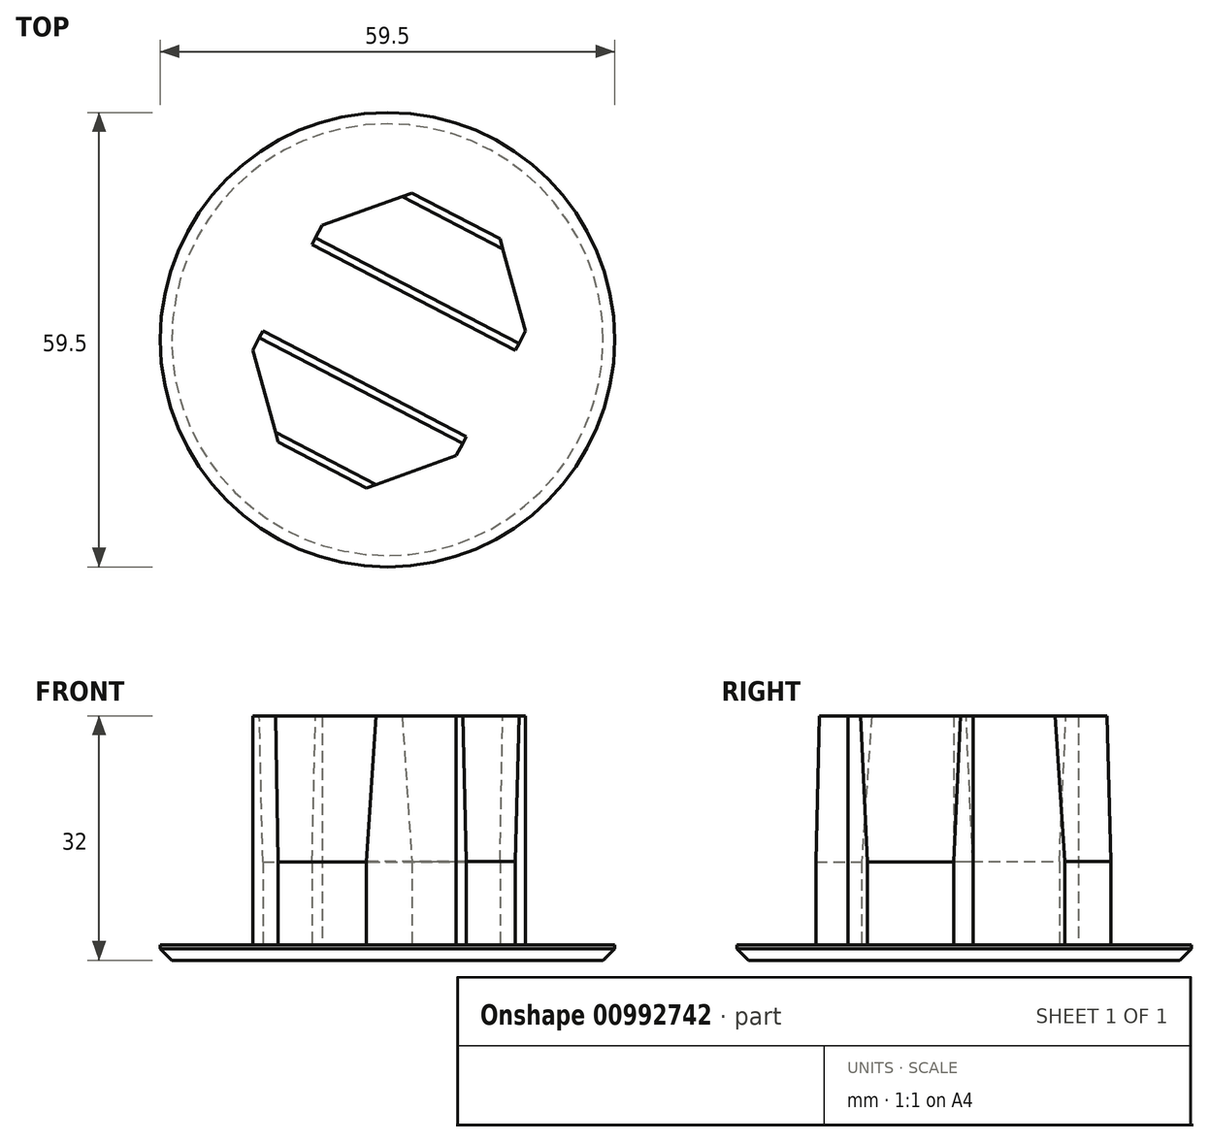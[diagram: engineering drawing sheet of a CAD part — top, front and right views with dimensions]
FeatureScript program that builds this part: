
annotation { "Feature Type Name" : "Feature", "Feature Type Description" : "" }
export const myFeature = defineFeature(function(context is Context, id is Id, definition is map)
    precondition{}
    {
        {
            var Q0;
            Q0=qCreatedBy(makeId("Top.planeOp"),FACE);
            var sketch = newSketch(context, id + "F0", { "sketchPlane" : qUnion([Q0])});
            skCircle(sketch, "E0", {"center": v(0, 0) * mm, "radius": 29.75 * mm});
            skSolve(sketch);
        }
        {
            var Q0;
            Q0 = qSketchRegion(id + "F0", true);
            extrude(context, id + "F1", {"entities" : qUnion([Q0]), "depth" : 2 * mm, "offsetDistance" : 25 * mm});
        }
        {
            var Q0;
            Q0=makeQuery(id+"F1.opExtrude","CAP_FACE",FACE,{"disambiguationData":[OSD([sQuery(id+"F0.wireOp",EDGE,"E0")])],"isStart":false});
            var sketch = newSketch(context, id + "F2", { "sketchPlane" : qUnion([Q0])});
            skLineSegment(sketch, "E1", {"start": v(-16.3, 1.14) * mm, "end": v(10.32, -12.68) * mm});
            skLineSegment(sketch, "E2", {"start": v(10.32, -12.68) * mm, "end": v(9.01, -15.2) * mm});
            skLineSegment(sketch, "E3", {"start": v(9.01, -15.2) * mm, "end": v(-2.76, -19.41) * mm});
            skLineSegment(sketch, "E4", {"start": v(-2.76, -19.41) * mm, "end": v(-14.3, -13.42) * mm});
            skLineSegment(sketch, "E5", {"start": v(-14.3, -13.42) * mm, "end": v(-17.61, -1.37) * mm});
            skLineSegment(sketch, "E6", {"start": v(-17.61, -1.37) * mm, "end": v(-16.3, 1.14) * mm});
            skLineSegment(sketch, "E7", {"start": v(-9.87, 12.45) * mm, "end": v(16.75, -1.37) * mm});
            skLineSegment(sketch, "E8", {"start": v(16.75, -1.37) * mm, "end": v(18.06, 1.14) * mm});
            skLineSegment(sketch, "E9", {"start": v(18.06, 1.14) * mm, "end": v(14.74, 13.2) * mm});
            skLineSegment(sketch, "E10", {"start": v(14.74, 13.2) * mm, "end": v(3.2, 19.18) * mm});
            skLineSegment(sketch, "E11", {"start": v(3.2, 19.18) * mm, "end": v(-8.57, 14.97) * mm});
            skLineSegment(sketch, "E12", {"start": v(-8.57, 14.97) * mm, "end": v(-9.87, 12.45) * mm});
            skSolve(sketch);
        }
        {
            var Q0;
            Q0 = qSketchRegion(id + "F2", true);
            extrude(context, id + "F3", {"entities" : qUnion([Q0]), "operationType" : NewBodyOperationType.ADD, "depth" : 30 * mm, "offsetDistance" : 25 * mm});
        }
        {
            var Q0;
            Q0=makeQuery(id+"F3.opExtrude","CAP_EDGE",EDGE,{"disambiguationData":[OSD([sQuery(id+"F2.wireOp",EDGE,"E7")])],"isStart":false});
            var Q1;
            Q1=makeQuery(id+"F3.opExtrude","CAP_EDGE",EDGE,{"disambiguationData":[OSD([sQuery(id+"F2.wireOp",EDGE,"E10")])],"isStart":false});
            chamfer(context, id + "F4", {"entities" : qUnion([Q0, Q1]), "chamferType" : ChamferType.OFFSET_ANGLE, "width" : 1 * mm, "oppositeDirection" : false, "angle" : 87 * degree, "tangentPropagation" : true});
        }
        {
            var Q0;
            Q0=makeQuery(id+"F3.opExtrude","CAP_EDGE",EDGE,{"disambiguationData":[OSD([sQuery(id+"F2.wireOp",EDGE,"E1")])],"isStart":false});
            var Q1;
            Q1=makeQuery(id+"F3.opExtrude","CAP_EDGE",EDGE,{"disambiguationData":[OSD([sQuery(id+"F2.wireOp",EDGE,"E4")])],"isStart":false});
            chamfer(context, id + "F5", {"entities" : qUnion([Q0, Q1]), "chamferType" : ChamferType.OFFSET_ANGLE, "width" : 19.1 * mm, "oppositeDirection" : false, "angle" : 3 * degree, "tangentPropagation" : true});
        }
        {
            var Q0;
            Q0=makeQuery(id+"F1.opExtrude","CAP_EDGE",EDGE,{"disambiguationData":[OSD([sQuery(id+"F0.wireOp",EDGE,"E0")])],"isStart":true});
            chamfer(context, id + "F6", {"entities" : qUnion([Q0]), "width" : 1.5 * mm, "tangentPropagation" : true});
        }
    });
